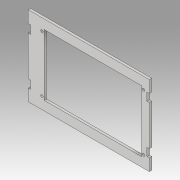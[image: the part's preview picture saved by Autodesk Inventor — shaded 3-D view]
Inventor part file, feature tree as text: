
AUTODESK INVENTOR PART (.ipt)
format: ipt  version: 2019.3 (Build 233278000, 278)  size: 127,488 bytes
history: native  units: mm
features: extrude x1, sketch x1
ambient origin geometry x8: Origin, YZ Plane, XZ Plane, XY Plane, X Axis, Y Axis, Z Axis, Center Point
bodies: Solid1 (feature_tree)
feature tree (2):
  extrude  "Extrusion1"  Depth=77.0mm
  sketch  "Sketch1"  dims[d0=122.0mm d1=77.0mm d3=10.0mm d5=11.5mm d6=3.1mm d7=127.6mm d8=63.8mm d9=70.6mm d10=3.2mm d11=3.2mm d12=3.0mm d13=0.0mm d14=100.0mm d15=11.5mm d16=152.0mm d17=20.0mm d18=3.0mm d19=10.0mm d20=15.0mm d21=15.0mm]
